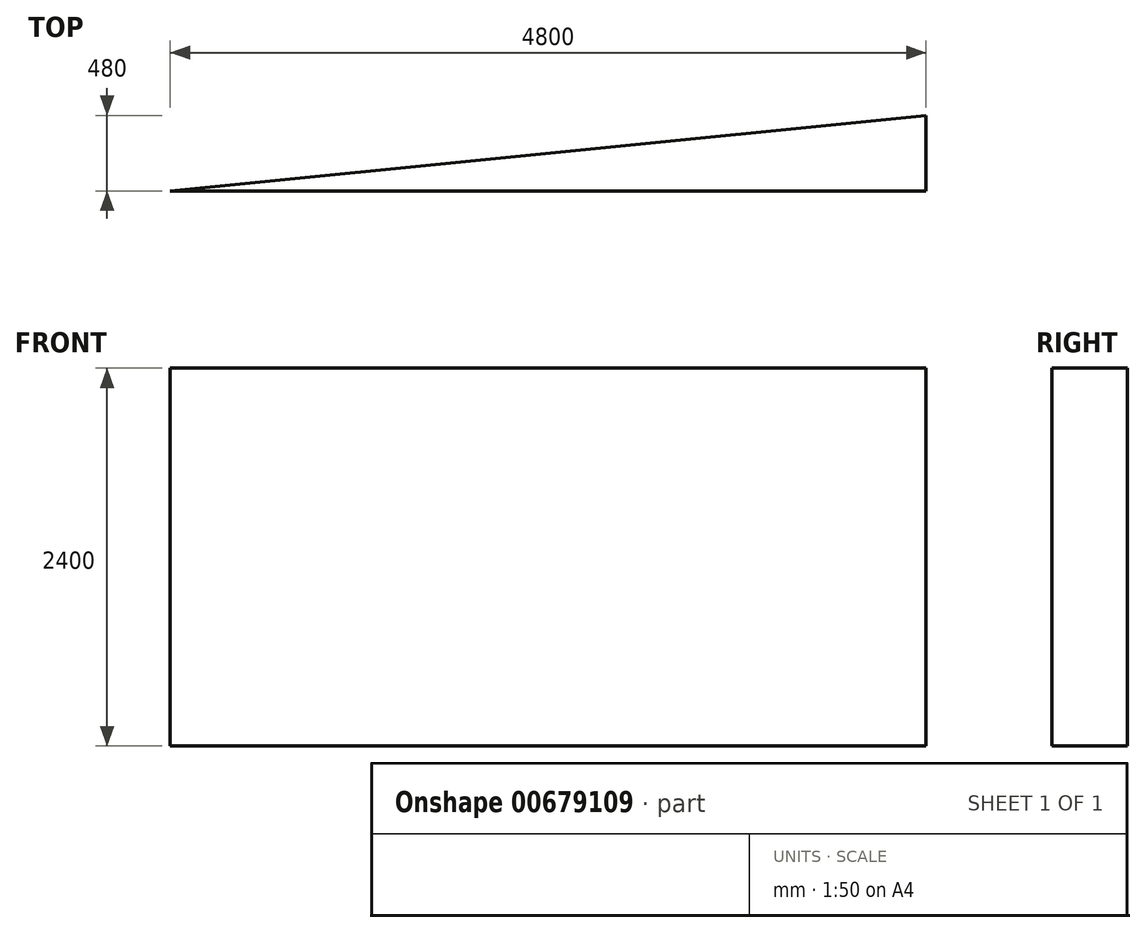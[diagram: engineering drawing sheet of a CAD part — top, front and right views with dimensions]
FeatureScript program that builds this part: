
annotation { "Feature Type Name" : "Feature", "Feature Type Description" : "" }
export const myFeature = defineFeature(function(context is Context, id is Id, definition is map)
    precondition{}
    {
        {
            var Q0;
            Q0=qCreatedBy(makeId("Top.planeOp"),FACE);
            var sketch = newSketch(context, id + "F0", { "sketchPlane" : qUnion([Q0])});
            skLineSegment(sketch, "E0.top", {"start": v(-2440.7, -486.06) * mm, "end": v(2359.3, -486.06) * mm});
            skLineSegment(sketch, "E0.right", {"start": v(2359.3, -6.06) * mm, "end": v(2359.3, -486.06) * mm});
            skLineSegment(sketch, "E1", {"start": v(-2440.7, -486.06) * mm, "end": v(2359.3, -6.06) * mm});
            skSolve(sketch);
        }
        {
            var Q0;
            Q0=makeQuery(id+"F0.imprint","IMPRINT",FACE,{"disambiguationData":[TD([[makeQuery(id+"F0.imprint","IMPRINT",EDGE,{"derivedFrom":sQuery(id+"F0.wireOp",EDGE,"E0.top")}),1.0]])]});
            extrude(context, id + "F1", {"entities" : qUnion([Q0]), "depth" : 2400 * mm, "offsetDistance" : 25 * mm});
        }
    });
